# Revit family: 201_PRW-_-B-_ +NKSD-C-_
name_source: partatom
category: Air Terminals
units: mm (PartAtom-declared; Revit-internal decimal feet)

## family parameters
Always vertical = Yes
Cut with Voids When Loaded = No
Part Type = Normal
Room Calculation Point = Yes
Round Connector Dimension = Use Diameter
Shared = No
Work Plane-Based = No

## types (7) — shared parameters
CAT0 = Yes
CL_Location_5000 = 5000 mm  [stored 16.4042 ft]
DZ = 2 mm  [stored 0.00656168 ft]
Description = EXPANSION BOXES TO BE MOUNTED UNDER THE NKSD-C, NKSD-CB, NK-SWB DIFFUSERS
L_ARR = 400 mm  [stored 1.31234 ft]
Manufacturer = Alnor
QmdConnectorList = 201;D
SW1 = Yes
SW2 = No
URL = http://www.ventilation-alnor.co.uk
W_ARR = 400 mm  [stored 1.31234 ft]
XRefLineVPlnId = 7453
YRefLineVPlnId = 7456
magiPartTypeId = 201
magiProductFamilyId = PRW-*-B-* +NKSD-C-*
zero-valued in all types: CLBTZ, H_ARR

## per-type parameters (varying)
| type | A2 | C1 | D | DPX | DPZ | DS2 |
| PRW-298-B-160 +NKSD-C-08 | 149 mm  [stored 0.488845 ft] | 250 mm  [stored 0.82021 ft] | 160 mm | 131 mm | 125 mm  [stored 0.410105 ft] | 131 mm |
| PRW-623-B-315 +NKSD-C-48 | 312 mm | 360 mm | 315 mm | 298 mm  [stored 0.97769 ft] | 180 mm | 298 mm  [stored 0.97769 ft] |
| PRW-623-B-315 +NKSD-C-24 | 312 mm | 360 mm | 315 mm | 298 mm  [stored 0.97769 ft] | 180 mm | 298 mm  [stored 0.97769 ft] |
| PRW-598-B-250 +NKSD-C-48 | 299 mm | 330 mm | 250 mm | 290 mm | 165 mm | 290 mm |
| PRW-598-B-250 +NKSD-C-24 | 299 mm | 330 mm | 250 mm | 281 mm | 165 mm | 281 mm |
| PRW-498-B-200 +NKSD-C-24 | 249 mm | 300 mm | 200 mm | 231 mm | 150 mm | 231 mm |
| PRW-396-B-200 +NKSD-C-16 | 198 mm | 300 mm | 200 mm | 184 mm | 150 mm | 184 mm |

note: column(s) folded — value = type name in every type: MC Product Code, magiProductId

note: [stored X ft] marks values corroborated as IEEE doubles in the binary element streams (Revit-internal decimal feet)

## geometry (parser evidence)
native form markers: Blend x4, Sweep x1
no freeform markers — native parametric forms only
